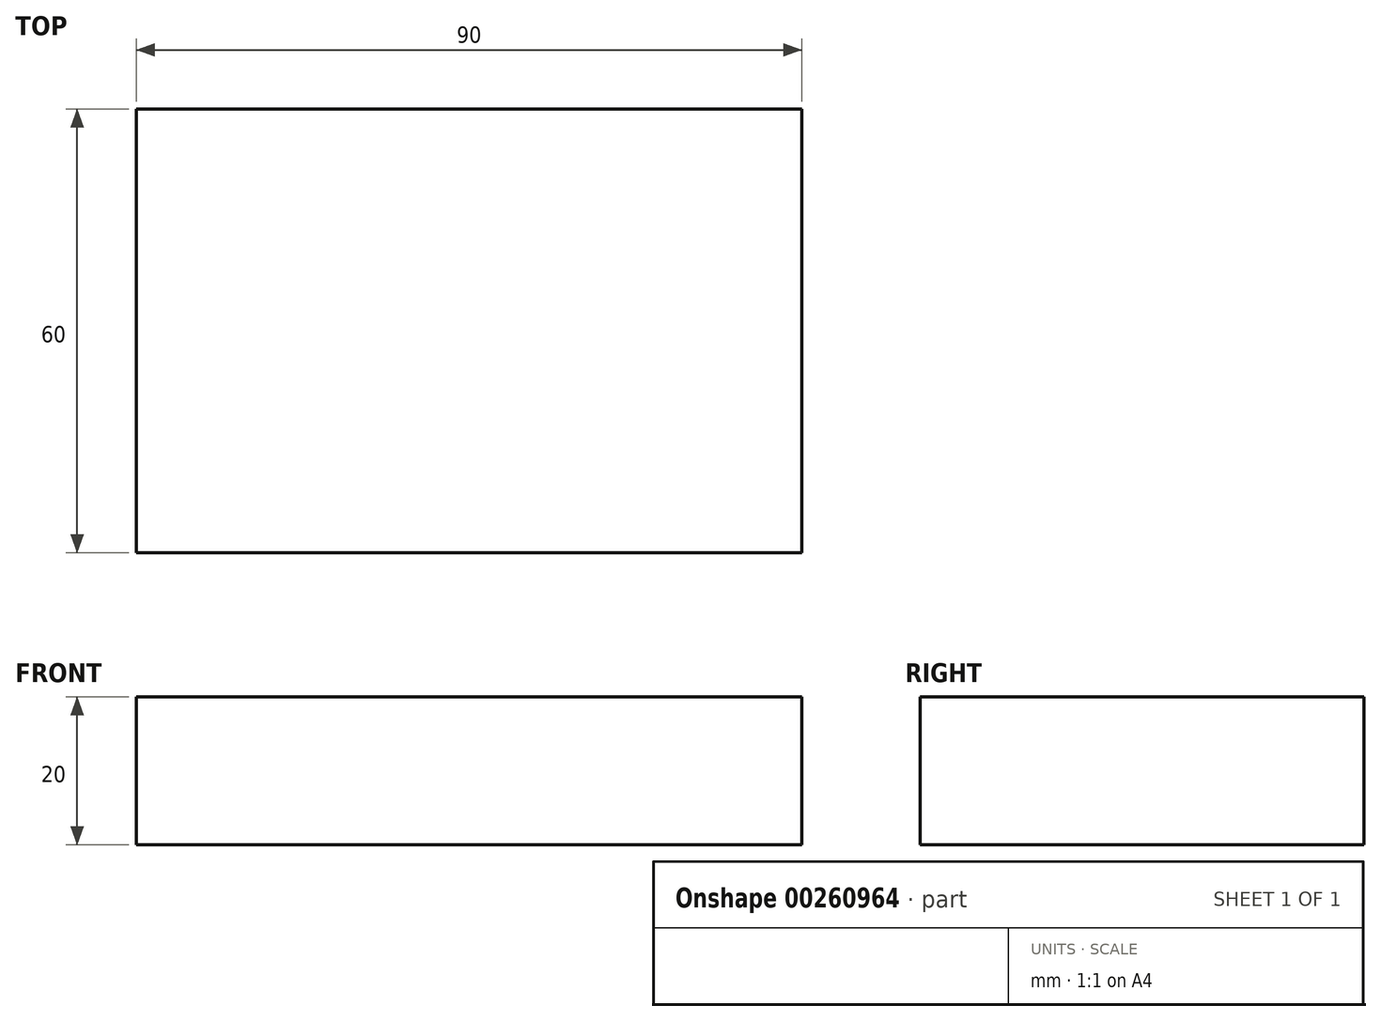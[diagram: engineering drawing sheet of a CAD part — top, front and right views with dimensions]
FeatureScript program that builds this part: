
annotation { "Feature Type Name" : "Feature", "Feature Type Description" : "" }
export const myFeature = defineFeature(function(context is Context, id is Id, definition is map)
    precondition{}
    {
        {
            var Q0;
            Q0=qCreatedBy(makeId("Top.planeOp"),FACE);
            var sketch = newSketch(context, id + "F0", { "sketchPlane" : qUnion([Q0])});
            skLineSegment(sketch, "E0.bottom", {"start": v(0, 0) * mm, "end": v(90, 0) * mm});
            skLineSegment(sketch, "E0.top", {"start": v(0, 60) * mm, "end": v(90, 60) * mm});
            skLineSegment(sketch, "E0.left", {"start": v(0, 0) * mm, "end": v(0, 60) * mm});
            skLineSegment(sketch, "E0.right", {"start": v(90, 0) * mm, "end": v(90, 60) * mm});
            skSolve(sketch);
        }
        {
            var Q0;
            Q0=makeQuery(id+"F0.imprint","IMPRINT",FACE,{"disambiguationData":[TD([[makeQuery(id+"F0.imprint","IMPRINT",EDGE,{"derivedFrom":sQuery(id+"F0.wireOp",EDGE,"E0.bottom")}),1.0]])]});
            extrude(context, id + "F1", {"entities" : qUnion([Q0]), "depth" : 20 * mm, "offsetDistance" : 25 * mm});
        }
    });
